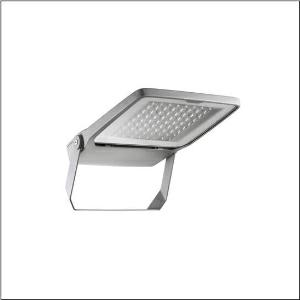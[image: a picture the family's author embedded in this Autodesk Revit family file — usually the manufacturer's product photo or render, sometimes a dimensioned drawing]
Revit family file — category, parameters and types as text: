
# Revit family: floodlight_fl_20_mini___pl52_5xa7671c2d1ac_f48d
name_source: partatom
category: Lighting Fixtures
units: mm (PartAtom-declared; Revit-internal decimal feet)

## family parameters
Cut with Voids When Loaded = No
Host = Face
Light Source = No
Part Type = Normal
Room Calculation Point = No
Round Connector Dimension = Use Diameter
Shared = No

## types (1)
- Floodlight FL 20 mini  PL52 (1 x LED 4000K / CRI = 70 (unbekannt), 12290 lm, 4000K)
    Apparent Load = 96 VA
    CIE Flux Codes = 27 59 98 100 100
    Color Rendering = 70
    Color Temperature = 4000K
    Default Elevation = 1800 mm
    Description = Floodlight FL 20 mini, floodlight, primary light control with lens, of plastic, primary optical cover: protective disc, of toughened safety glass, transparent, light distribution: PL52, light emission: direct distribution, primary light characteristic: asymmetric, installation type: surface-mounted, LED, High Power LED, rated luminous flux: 12.290lm, luminous efficacy: 128lm/W, light colour: 740, colour temperature: 4000K, control gear: ECG Basic, control: power reduction, overheat protection, electronic power reduction, with terminal, 5-pole, max. 2.5mm², mains connection: 220..240V, AC, 50/60Hz, rated input power: 96W, LED unit, of diecast aluminium, powder-coated, Siteco® metallic grey (DB 702S), corrosivity category C5 mid according to DIN EN ISO 12944, incl. 1x M20 cable gland for cable Ø 6.5..12mm, length: 446mm, width: 355mm, height: 62mm, housing frame, of diecast aluminium, powder-coated, Siteco® metallic grey (DB 702S), mounting bracket, of steel, powder-coated, Siteco® metallic grey (DB 702S), ON/OFF, protection rating (complete): IP66, insulation class (complete): insulation class I (protective earthing), certification: CE, ENEC, VDE, protection symbol: D, permissible operating ambient temperature: -40..+40°C, permissible operating ambient temperature for outdoor applications: -40..+50°C, standard: DIN EN 12944, packaging unit: 1 piece

Light Distribution: PL52
    Height = 62 mm  [stored 0.203412 ft]
    Lamp = 1 x LED 4000K / CRI >= 70 (unbekannt)
    Lamp Light Flux = 12290 lm
    Lamp count = 1
    Length = 467 mm
    Luminous efficacy = 128 lm/W
    Manufacturer = Siteco
    ModVariant = No
    Model = 5XA7671C2D1AC
    Mounting Place = Wall
    Mounting Type = Surface mounted
    Number of Poles = 1
    OnlyDefault = Yes
    Power Factor = 1
    Product Name = Floodlight FL 20 mini | PL52
    Product group = floodlight | wall mounted
    ProductGroupID = 2001
    Protection Class = Protection class I
    Protection Degree = IP 66
    RLX_Detail_Level = 1
    RLX_Emergency_Light_Flux = 0 lm
    RLX_Emergency_Type = 0
    RLX_Emergency_Type_DB = No
    RlxData = <blob elided: 71101 chars, md5=489289ba>
    Socket = socket
    Standby Power = 0 W
    System Light Flux = 12290 lm
    System Power = 96 W
    Type Comments = Product without accessories
    Type Image = l_1005948.jpg
    URL = http://relux.com
    VarID = ---
    Voltage = 0 V
    Weight = 0.00 kg
    Width = 335 mm

note: [stored X ft] marks values corroborated as IEEE doubles in the binary element streams (Revit-internal decimal feet)

## geometry (parser evidence)
native form markers: Blend x4, Sweep x11
no freeform markers — native parametric forms only
